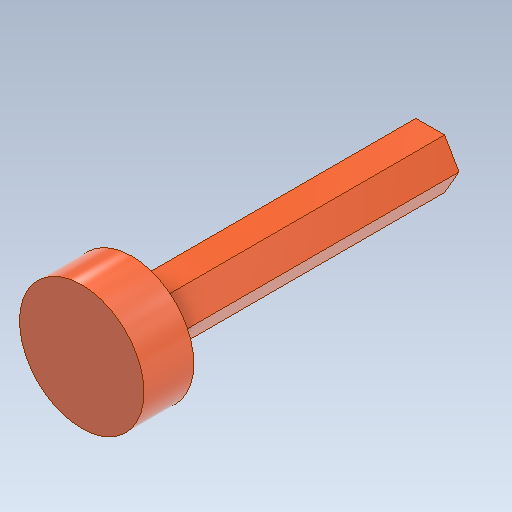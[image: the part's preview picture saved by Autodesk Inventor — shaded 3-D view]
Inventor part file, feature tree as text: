
AUTODESK INVENTOR PART (.ipt)
format: ipt  version: 2021.2 (Build 252289000, 289)  size: 103,936 bytes
history: native  units: in
note: dims shown in document units (in); Inventor stores cm internally (conversion verified against a paired STEP export)
features: other x3, sketch x2
ambient origin geometry x8: Origin, YZ Plane, XZ Plane, XY Plane, X Axis, Y Axis, Z Axis, Center Point
bodies: Solid1 (feature_tree)
feature tree (5):
  other  "1_2x3-inchHexShaft.ipt"
  other  "Solid1::1_2x3-inchHexShaft.ipt"
  other  "TaggingFeature1"
  sketch  "Sketch1"  dims[d0=0.3937in]
  sketch  "Sketch2"
